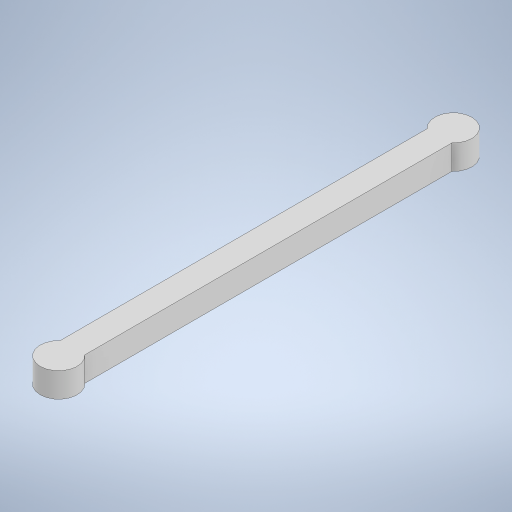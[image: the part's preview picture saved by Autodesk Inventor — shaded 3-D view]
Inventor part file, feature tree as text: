
AUTODESK INVENTOR PART (.ipt)
format: ipt  version: 2024.3 (Build 283343000, 343)  size: 239,104 bytes
history: native  units: mm
features: other x1, extrude x1, sketch x1
ambient origin geometry x8: Origin, YZ Plane, XZ Plane, XY Plane, X Axis, Y Axis, Z Axis, Center Point
bodies: Body1 (feature_tree)
feature tree (3):
  other  "ソリッド1"
  extrude  "押し出し1"  Depth=160.0mm
  sketch  "スケッチ1"
